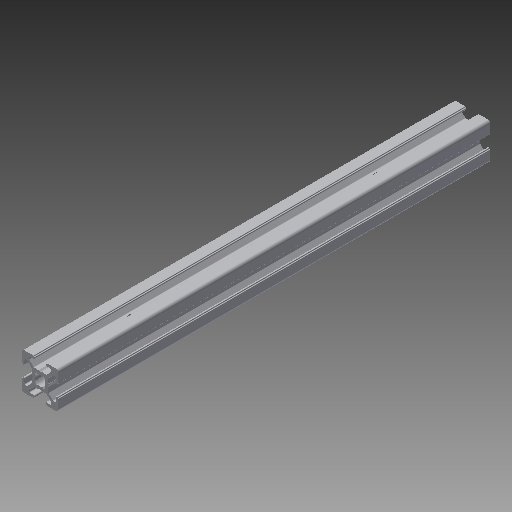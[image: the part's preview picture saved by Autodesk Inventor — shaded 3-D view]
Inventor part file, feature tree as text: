
AUTODESK INVENTOR PART (.ipt)
format: ipt  version: 2017 (Build 210142000, 142)  size: 410,112 bytes
history: native  units: in
note: dims shown in document units (in); Inventor stores cm internally (conversion verified against a paired STEP export)
features: other x3, sketch x2, extrude x1, hole x1, mirror x1
ambient origin geometry x8: Origin, YZ Plane, XZ Plane, XY Plane, X Axis, Y Axis, Z Axis, Center Point
bodies: Solid1 (feature_tree)
feature tree (8):
  other  "Blocks"
  extrude  "Extrusion1"  Depth=2.0in
  hole  "Hole1"  [1 undecoded]
  mirror  "Mirror1"
  sketch  "Sketch1"  dims[d1=0.0in d5=2.0in]
  other  "20x20"
  sketch  "Sketch3"  dims[d6=0.187in d7=0.75in d8=0.375in d9=0.25in d10=0.5635in d11=1.0in d12=0.8108in d13=1.0in d14=1.0in]
  other  "20x20:1"
note: 1 required parameter value undecoded (feature->parameter linkage not recoverable at this tier; creation-order binding heuristic only, values carry confidence <= 0.55)
